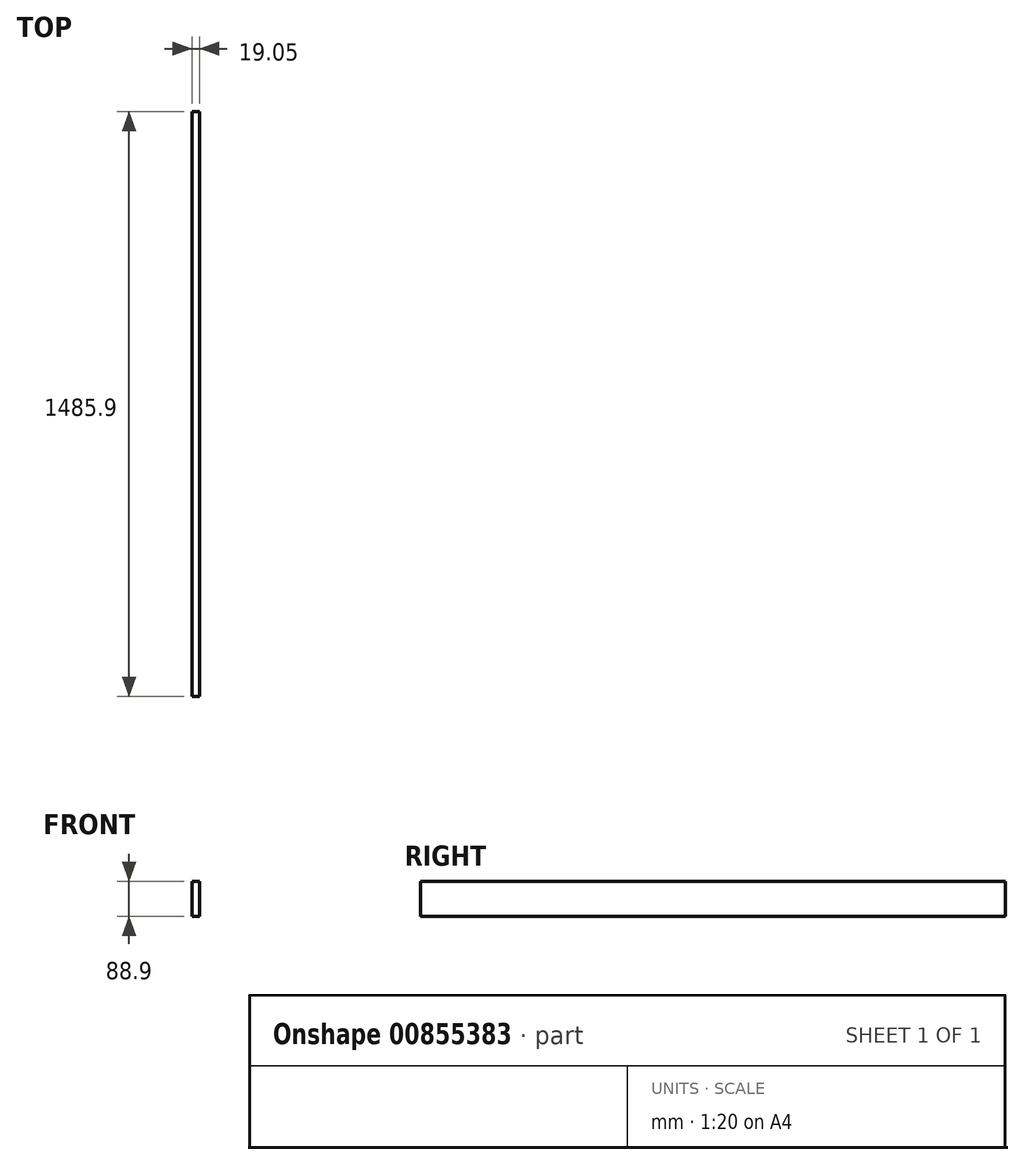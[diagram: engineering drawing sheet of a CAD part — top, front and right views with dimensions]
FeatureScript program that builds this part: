
annotation { "Feature Type Name" : "Feature", "Feature Type Description" : "" }
export const myFeature = defineFeature(function(context is Context, id is Id, definition is map)
    precondition{}
    {
        {
            var Q0;
            Q0=qCreatedBy(makeId("Front.planeOp"),FACE);
            var sketch = newSketch(context, id + "F0", { "sketchPlane" : qUnion([Q0])});
            skLineSegment(sketch, "E0.bottom", {"start": v(0, 0) * mm, "end": v(19.05, 0) * mm});
            skLineSegment(sketch, "E0.top", {"start": v(0, 88.9) * mm, "end": v(19.05, 88.9) * mm});
            skLineSegment(sketch, "E0.left", {"start": v(0, 0) * mm, "end": v(0, 88.9) * mm});
            skLineSegment(sketch, "E0.right", {"start": v(19.05, 0) * mm, "end": v(19.05, 88.9) * mm});
            skSolve(sketch);
        }
        {
            var Q0;
            Q0 = qSketchRegion(id + "F0", true);
            extrude(context, id + "F1", {"entities" : qUnion([Q0]), "depth" : 1485.9 * mm, "offsetDistance" : 25.4 * mm});
        }
    });
